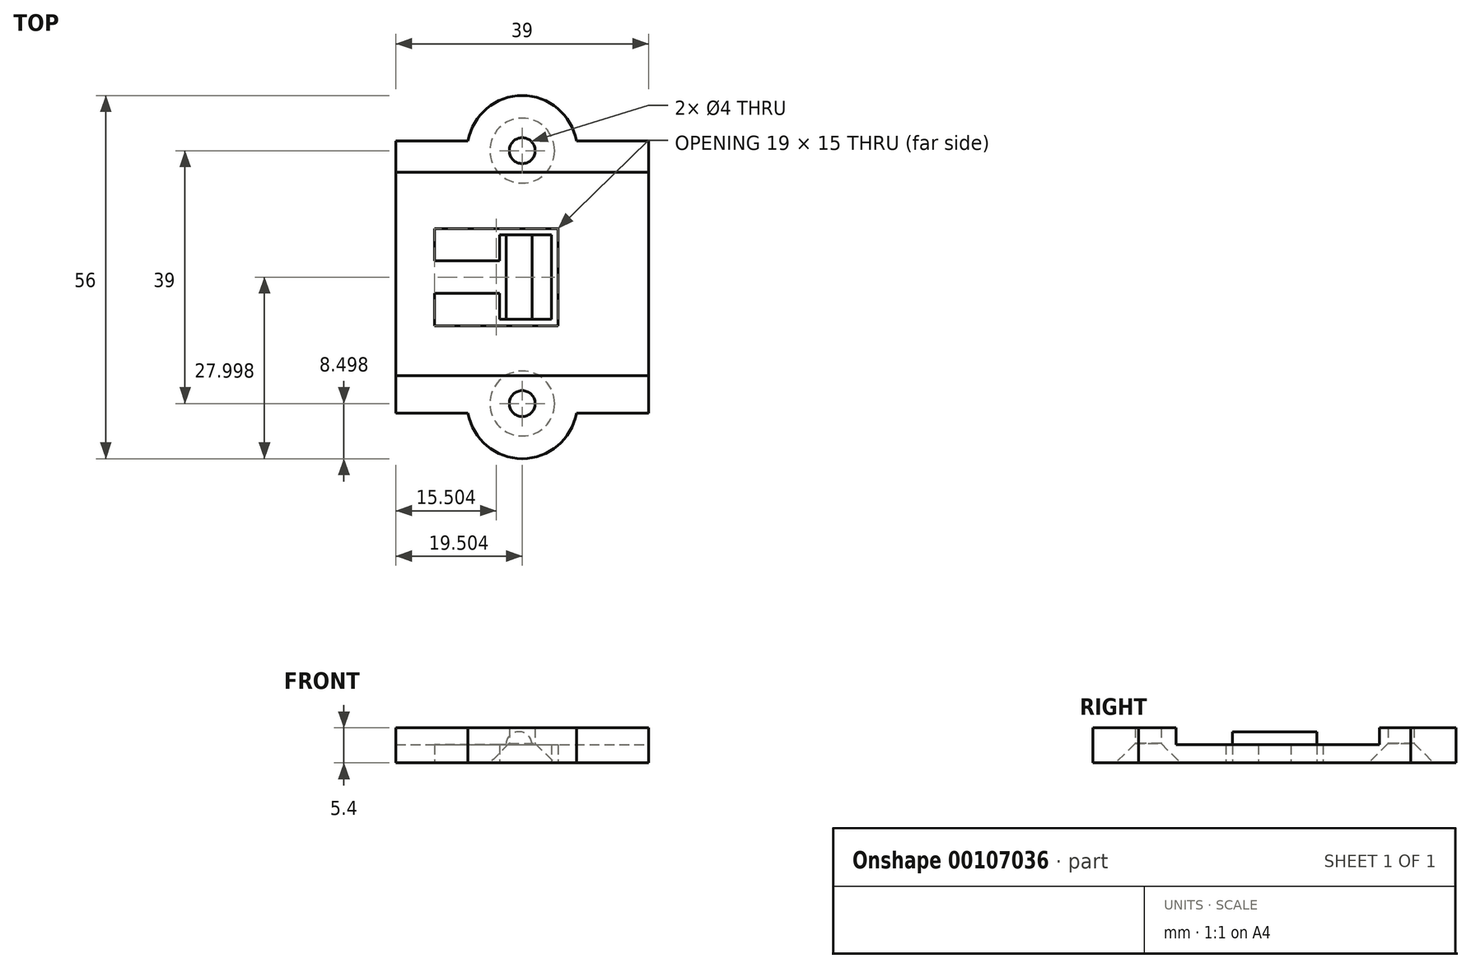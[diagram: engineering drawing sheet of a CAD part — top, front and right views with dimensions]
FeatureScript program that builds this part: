
annotation { "Feature Type Name" : "Feature", "Feature Type Description" : "" }
export const myFeature = defineFeature(function(context is Context, id is Id, definition is map)
    precondition{}
    {
        {
            var Q0;
            Q0=qCreatedBy(makeId("Top.planeOp"),FACE);
            var sketch = newSketch(context, id + "F0", { "sketchPlane" : qUnion([Q0])});
            skLineSegment(sketch, "E0.bottom", {"start": v(-8.3, 16.03) * mm, "end": v(30.7, 16.03) * mm});
            skLineSegment(sketch, "E0.top", {"start": v(-8.3, -25.97) * mm, "end": v(30.7, -25.97) * mm});
            skLineSegment(sketch, "E0.left", {"start": v(-8.3, 16.03) * mm, "end": v(-8.3, -25.97) * mm});
            skLineSegment(sketch, "E0.right", {"start": v(30.7, 16.03) * mm, "end": v(30.7, -25.97) * mm});
            skPoint(sketch, "E1", {"position": v(11.2, 14.53) * mm});
            skPoint(sketch, "E2", {"position": v(11.2, -24.47) * mm});
            skPoint(sketch, "E3", {"position": v(11.2, -4.97) * mm});
            skPoint(sketch, "E3.positionSnap0", {"position": v(-8.3, -4.97) * mm});
            skCircle(sketch, "E4", {"center": v(11.2, 14.53) * mm, "radius": 8.5 * mm});
            skCircle(sketch, "E5", {"center": v(11.2, -24.47) * mm, "radius": 8.5 * mm});
            skLineSegment(sketch, "E6", {"start": v(7.7, 1.53) * mm, "end": v(7.7, -11.47) * mm});
            skLineSegment(sketch, "E7", {"start": v(7.7, 1.53) * mm, "end": v(15.7, 1.53) * mm});
            skLineSegment(sketch, "E8", {"start": v(15.7, 1.53) * mm, "end": v(15.7, -11.47) * mm});
            skLineSegment(sketch, "E9", {"start": v(15.7, -11.47) * mm, "end": v(7.7, -11.47) * mm});
            skLineSegment(sketch, "E10", {"start": v(16.7, -11.47) * mm, "end": v(16.7, 1.53) * mm});
            skLineSegment(sketch, "E11", {"start": v(16.7, 1.53) * mm, "end": v(16.7, 2.53) * mm});
            skLineSegment(sketch, "E12", {"start": v(16.7, 2.53) * mm, "end": v(7.7, 2.53) * mm});
            skLineSegment(sketch, "E13", {"start": v(16.7, -11.47) * mm, "end": v(16.7, -12.47) * mm});
            skLineSegment(sketch, "E14", {"start": v(16.7, -12.47) * mm, "end": v(7.7, -12.47) * mm});
            skLineSegment(sketch, "E15", {"start": v(7.7, -12.47) * mm, "end": v(-2.3, -12.47) * mm});
            skLineSegment(sketch, "E16", {"start": v(-2.3, -12.47) * mm, "end": v(-2.3, -7.47) * mm});
            skLineSegment(sketch, "E17", {"start": v(-2.3, -7.47) * mm, "end": v(7.7, -7.47) * mm});
            skLineSegment(sketch, "E18", {"start": v(7.7, 2.53) * mm, "end": v(-2.3, 2.53) * mm});
            skLineSegment(sketch, "E19", {"start": v(-2.3, 2.53) * mm, "end": v(-2.3, -2.47) * mm});
            skLineSegment(sketch, "E20", {"start": v(-2.3, -2.47) * mm, "end": v(7.7, -2.47) * mm});
            skSolve(sketch);
        }
        {
            var Q0;
            {var subQ0=sQuery(id+"F0.wireOp",EDGE,"E4");var subQ1=sQuery(id+"F0.wireOp",EDGE,"E0.bottom");var subQ2=makeQuery(id+"F0.imprint","INTERSECT",VERTEX,{"disambiguationData":[OD(0.0)],"derivedFrom":[subQ1,subQ0]});Q0=makeQuery(id+"F0.imprint","IMPRINT",FACE,{"disambiguationData":[TD([[makeQuery(id+"F0.imprint","IMPRINT",EDGE,{"disambiguationData":[TD([[subQ2,-1.0]])],"derivedFrom":subQ1}),1.0]])]});}
            var Q1;
            {var subQ0=sQuery(id+"F0.wireOp",EDGE,"E5");var subQ1=sQuery(id+"F0.wireOp",EDGE,"E0.top");var subQ2=makeQuery(id+"F0.imprint","INTERSECT",VERTEX,{"disambiguationData":[OD(0.0)],"derivedFrom":[subQ1,subQ0]});Q1=makeQuery(id+"F0.imprint","IMPRINT",FACE,{"disambiguationData":[TD([[makeQuery(id+"F0.imprint","IMPRINT",EDGE,{"disambiguationData":[TD([[subQ2,-1.0]])],"derivedFrom":subQ1}),-1.0]])]});}
            var Q2;
            {var subQ5=sQuery(id+"F0.wireOp",EDGE,"E0.left");Q2=makeQuery(id+"F0.imprint","IMPRINT",FACE,{"disambiguationData":[TD([[makeQuery(id+"F0.imprint","IMPRINT",EDGE,{"derivedFrom":subQ5}),1.0]])]});}
            var Q3;
            {var subQ0=sQuery(id+"F0.wireOp",EDGE,"E5");var subQ1=sQuery(id+"F0.wireOp",EDGE,"E0.top");var subQ2=makeQuery(id+"F0.imprint","INTERSECT",VERTEX,{"disambiguationData":[OD(0.0)],"derivedFrom":[subQ1,subQ0]});Q3=makeQuery(id+"F0.imprint","IMPRINT",FACE,{"disambiguationData":[TD([[makeQuery(id+"F0.imprint","IMPRINT",EDGE,{"disambiguationData":[TD([[subQ2,-1.0]])],"derivedFrom":subQ1}),1.0]])]});}
            var Q4;
            {var subQ0=sQuery(id+"F0.wireOp",EDGE,"E4");var subQ1=sQuery(id+"F0.wireOp",EDGE,"E0.bottom");var subQ2=makeQuery(id+"F0.imprint","INTERSECT",VERTEX,{"disambiguationData":[OD(0.0)],"derivedFrom":[subQ1,subQ0]});Q4=makeQuery(id+"F0.imprint","IMPRINT",FACE,{"disambiguationData":[TD([[makeQuery(id+"F0.imprint","IMPRINT",EDGE,{"disambiguationData":[TD([[subQ2,-1.0]])],"derivedFrom":subQ1}),-1.0]])]});}
            var Q5;
            {var subQ0=sQuery(id+"F0.wireOp",EDGE,"E7");Q5=makeQuery(id+"F0.imprint","IMPRINT",FACE,{"disambiguationData":[TD([[makeQuery(id+"F0.imprint","IMPRINT",EDGE,{"derivedFrom":subQ0}),-1.0]])]});}
            extrude(context, id + "F1", {"entities" : qUnion([Q0, Q1, Q2, Q3, Q4, Q5]), "depth" : 5.4 * mm});
        }
        {
            var Q0;
            Q0=makeQuery(id+"F1.opExtrude","SWEPT_FACE",FACE,{"disambiguationData":[OSD([sQuery(id+"F0.wireOp",EDGE,"E0.right")])]});
            var sketch = newSketch(context, id + "F2", { "sketchPlane" : qUnion([Q0])});
            skPoint(sketch, "E21", {"position": v(-4.97, 5.4) * mm});
            skPoint(sketch, "E22", {"position": v(-20.17, 5.4) * mm});
            skPoint(sketch, "E23", {"position": v(11.23, 5.4) * mm});
            skLineSegment(sketch, "E24", {"start": v(-20.17, 5.4) * mm, "end": v(-20.17, 2.8) * mm});
            skLineSegment(sketch, "E25", {"start": v(-20.17, 2.8) * mm, "end": v(11.23, 2.8) * mm});
            skLineSegment(sketch, "E26", {"start": v(11.23, 2.8) * mm, "end": v(11.23, 5.4) * mm});
            skLineSegment(sketch, "E27", {"start": v(-20.17, 5.4) * mm, "end": v(11.23, 5.4) * mm});
            skSolve(sketch);
        }
        {
            var Q0;
            Q0=makeQuery(id+"F2.imprint","IMPRINT",FACE,{"disambiguationData":[TD([[makeQuery(id+"F2.imprint","IMPRINT",EDGE,{"derivedFrom":sQuery(id+"F2.wireOp",EDGE,"E24")}),1.0]])]});
            extrude(context, id + "F3", {"entities" : qUnion([Q0]), "operationType" : NewBodyOperationType.REMOVE, "oppositeDirection" : true, "depth" : 40 * mm});
        }
        {
            var Q0;
            Q0=makeQuery(id+"F3.boolean.opBoolean","COPY",FACE,{"derivedFrom":makeQuery(id+"F3.opExtrude","SWEPT_FACE",FACE,{"disambiguationData":[OSD([sQuery(id+"F2.wireOp",EDGE,"E25")])]})});
            var sketch = newSketch(context, id + "F4", { "sketchPlane" : qUnion([Q0])});
            skLineSegment(sketch, "E28", {"start": v(8.7, 1.53) * mm, "end": v(8.7, -11.47) * mm});
            skLineSegment(sketch, "E29", {"start": v(8.7, -11.47) * mm, "end": v(10.7, -11.47) * mm});
            skLineSegment(sketch, "E30", {"start": v(10.7, -11.47) * mm, "end": v(10.7, 1.53) * mm});
            skLineSegment(sketch, "E31", {"start": v(10.7, 1.53) * mm, "end": v(8.7, 1.53) * mm});
            skSolve(sketch);
        }
        {
            var Q0;
            Q0=makeQuery(id+"F4.imprint","IMPRINT",FACE,{"disambiguationData":[TD([[makeQuery(id+"F4.imprint","IMPRINT",EDGE,{"derivedFrom":sQuery(id+"F4.wireOp",EDGE,"E28")}),1.0]])]});
            var Q1;
            Q1=sQuery(id+"F4.wireOp",EDGE,"E30");
            revolve(context, id + "F5", {"operationType" : NewBodyOperationType.ADD, "entities" : qUnion([Q0]), "axis" : qUnion([Q1]), "revolveType" : RevolveType.FULL});
        }
        {
            var Q0;
            Q0=sQuery(id+"F0.wireOp",VERTEX,"E2");
            var Q1;
            Q1=sQuery(id+"F0.wireOp",VERTEX,"E1");
            var Q2;
            Q2=makeQuery(id+"F1.opExtrude","SWEPT_BODY",BODY,{"disambiguationData":[OSD([sQuery(id+"F0.wireOp",EDGE,"E0.bottom"),sQuery(id+"F0.wireOp",EDGE,"E0.top"),sQuery(id+"F0.wireOp",EDGE,"E0.left"),sQuery(id+"F0.wireOp",EDGE,"E0.right"),sQuery(id+"F0.wireOp",EDGE,"E4"),sQuery(id+"F0.wireOp",EDGE,"E5"),sQuery(id+"F0.wireOp",EDGE,"E6"),sQuery(id+"F0.wireOp",EDGE,"E7"),sQuery(id+"F0.wireOp",EDGE,"E8"),sQuery(id+"F0.wireOp",EDGE,"E9"),sQuery(id+"F0.wireOp",EDGE,"E10"),sQuery(id+"F0.wireOp",EDGE,"E11"),sQuery(id+"F0.wireOp",EDGE,"E12"),sQuery(id+"F0.wireOp",EDGE,"E13"),sQuery(id+"F0.wireOp",EDGE,"E14"),sQuery(id+"F0.wireOp",EDGE,"E15"),sQuery(id+"F0.wireOp",EDGE,"E16"),sQuery(id+"F0.wireOp",EDGE,"E17"),sQuery(id+"F0.wireOp",EDGE,"E18"),sQuery(id+"F0.wireOp",EDGE,"E19"),sQuery(id+"F0.wireOp",EDGE,"E20")])]});
            hole(context, id + "F6", {"style" : HoleStyle.C_SINK, "endStyle" : HoleEndStyle.THROUGH, "oppositeDirection" : true, "holeDiameter" : 4 * mm, "cSinkDiameter" : 10 * mm, "cSinkAngle" : 90 * degree, "locations" : qUnion([Q0, Q1]), "scope" : qUnion([Q2]), "isTappedThrough" : true});
        }
    });
